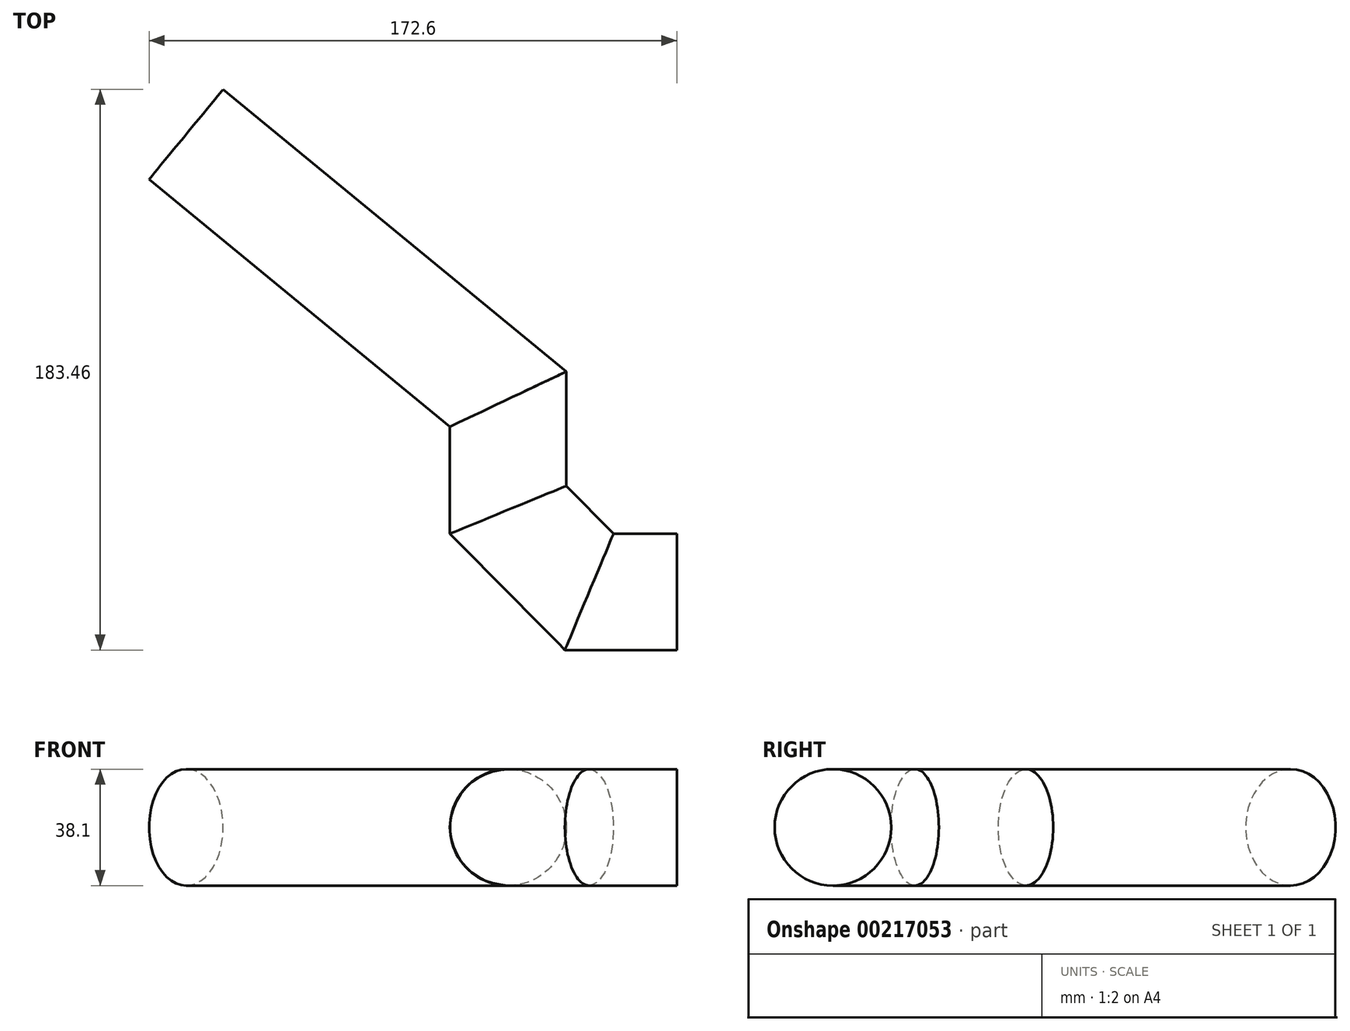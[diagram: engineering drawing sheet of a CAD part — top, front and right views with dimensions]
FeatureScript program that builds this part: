
annotation { "Feature Type Name" : "Feature", "Feature Type Description" : "" }
export const myFeature = defineFeature(function(context is Context, id is Id, definition is map)
    precondition{}
    {
        {
            var Q0;
            Q0=qCreatedBy(makeId("Top.planeOp"),FACE);
            var sketch = newSketch(context, id + "F0", { "sketchPlane" : qUnion([Q0])});
            skLineSegment(sketch, "E0", {"start": v(-1.04, -92.55) * mm, "end": v(-28.57, -92.55) * mm});
            skLineSegment(sketch, "E1", {"start": v(-28.57, -92.55) * mm, "end": v(-54.97, -65.85) * mm});
            skLineSegment(sketch, "E2", {"start": v(-54.97, -65.85) * mm, "end": v(-54.97, -29.6) * mm});
            skLineSegment(sketch, "E3", {"start": v(-54.97, -29.6) * mm, "end": v(-82.7, -6.8) * mm});
            skSolve(sketch);
        }
        {
            var Q0;
            Q0=qCreatedBy(makeId("Right.planeOp"),FACE);
            var sketch = newSketch(context, id + "F1", { "sketchPlane" : qUnion([Q0])});
            skCircle(sketch, "E4", {"center": v(-92.76, 0) * mm, "radius": 19.05 * mm});
            skSolve(sketch);
        }
        {
            var Q0;
            Q0=makeQuery(id+"F1.imprint","IMPRINT",FACE,{"disambiguationData":[TD([[makeQuery(id+"F1.imprint","IMPRINT",EDGE,{"derivedFrom":sQuery(id+"F1.wireOp",EDGE,"E4")}),1.0]])]});
            var Q1;
            Q1=sQuery(id+"F0.wireOp",EDGE,"E0");
            var Q2;
            Q2=sQuery(id+"F0.wireOp",EDGE,"E1");
            var Q3;
            Q3=sQuery(id+"F0.wireOp",EDGE,"E2");
            var Q4;
            Q4=sQuery(id+"F0.wireOp",EDGE,"E3");
            sweep(context, id + "F2", {"profiles" : qUnion([Q0]), "path" : qUnion([Q1, Q2, Q3, Q4])});
        }
        {
            var Q0;
            Q0=makeQuery(id+"F2.opSweep","CAP_FACE",FACE,{"disambiguationData":[OSD([sQuery(id+"F0.wireOp",VERTEX,"E3.end"),sQuery(id+"F1.wireOp",EDGE,"E4")])],"isStart":false});
            extrude(context, id + "F3", {"entities" : qUnion([Q0]), "operationType" : NewBodyOperationType.ADD, "depth" : 76.2 * mm});
        }
        {
            var Q0;
            Q0=makeQuery(id+"F3.opExtrude","CAP_FACE",FACE,{"disambiguationData":[OSD([sQuery(id+"F0.wireOp",VERTEX,"E3.end"),sQuery(id+"F1.wireOp",EDGE,"E4")])],"isStart":false});
            extrude(context, id + "F4", {"entities" : qUnion([Q0]), "operationType" : NewBodyOperationType.ADD, "depth" : 25.4 * mm});
        }
    });
